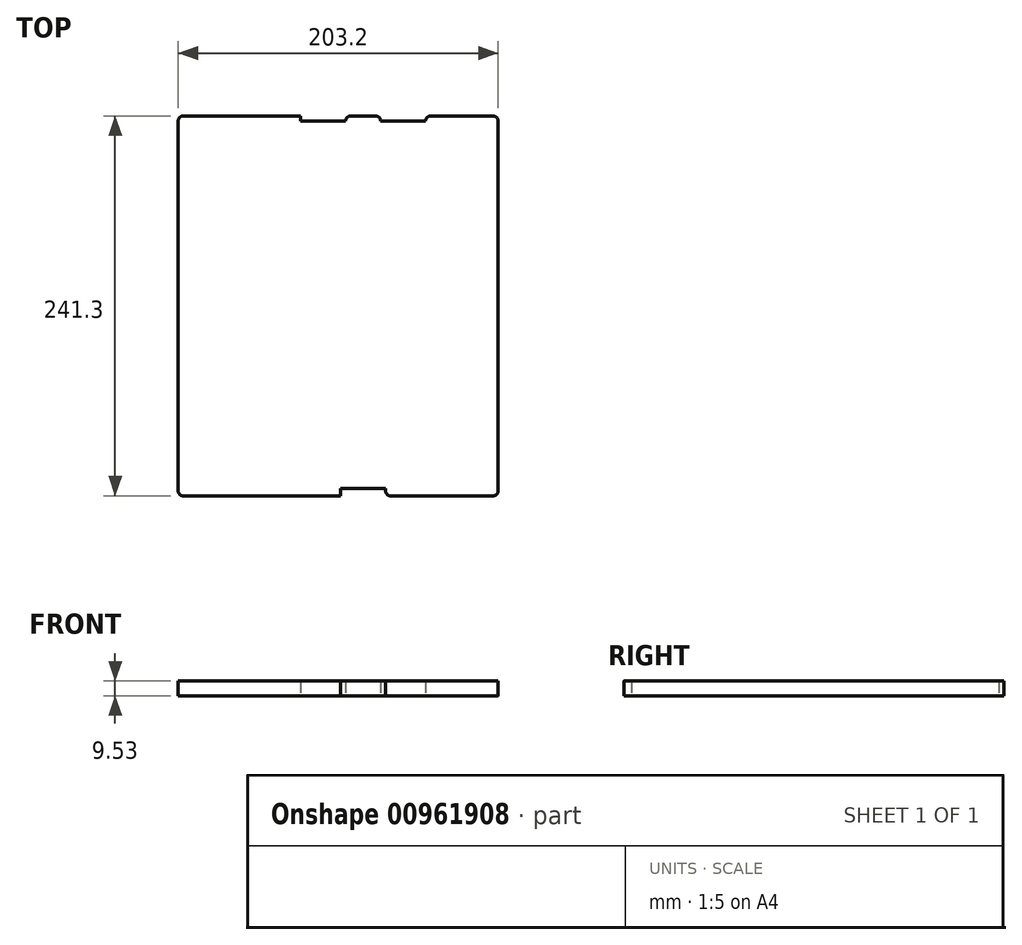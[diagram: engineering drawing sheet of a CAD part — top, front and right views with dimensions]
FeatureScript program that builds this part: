
annotation { "Feature Type Name" : "Feature", "Feature Type Description" : "" }
export const myFeature = defineFeature(function(context is Context, id is Id, definition is map)
    precondition{}
    {
        {
            var Q0;
            Q0=qCreatedBy(makeId("Top.planeOp"),FACE);
            var sketch = newSketch(context, id + "F0", { "sketchPlane" : qUnion([Q0])});
            skLineSegment(sketch, "E0.bottom", {"start": v(101.6, 120.65) * mm, "end": v(-101.6, 120.65) * mm});
            skLineSegment(sketch, "E0.top", {"start": v(101.6, -120.65) * mm, "end": v(-101.6, -120.65) * mm});
            skLineSegment(sketch, "E0.left", {"start": v(101.6, 120.65) * mm, "end": v(101.6, -120.65) * mm});
            skLineSegment(sketch, "E0.right", {"start": v(-101.6, 120.65) * mm, "end": v(-101.6, -120.65) * mm});
            skPoint(sketch, "E0.middle", {"position": v(0, 0) * mm});
            skSolve(sketch);
        }
        {
            var Q0;
            Q0=makeQuery(id+"F0.imprint","IMPRINT",FACE,{"disambiguationData":[TD([[makeQuery(id+"F0.imprint","IMPRINT",EDGE,{"derivedFrom":sQuery(id+"F0.wireOp",EDGE,"E0.bottom")}),1.0]])]});
            extrude(context, id + "F1", {"entities" : qUnion([Q0]), "depth" : 9.52 * mm, "offsetDistance" : 25.4 * mm});
        }
        {
            var Q0;
            Q0=makeQuery(id+"F1.opExtrude","SWEPT_FACE",FACE,{"disambiguationData":[OSD([sQuery(id+"F0.wireOp",EDGE,"E0.top")])]});
            var sketch = newSketch(context, id + "F2", { "sketchPlane" : qUnion([Q0])});
            skLineSegment(sketch, "E1.bottom", {"start": v(1.59, 9.53) * mm, "end": v(30.16, 9.53) * mm});
            skLineSegment(sketch, "E1.top", {"start": v(1.59, 0) * mm, "end": v(30.16, 0) * mm});
            skLineSegment(sketch, "E1.left", {"start": v(1.59, 9.53) * mm, "end": v(1.59, 0) * mm});
            skLineSegment(sketch, "E1.right", {"start": v(30.16, 9.53) * mm, "end": v(30.16, 0) * mm});
            skSolve(sketch);
        }
        {
            var Q0;
            Q0 = qSketchRegion(id + "F2", true);
            extrude(context, id + "F3", {"entities" : qUnion([Q0]), "operationType" : NewBodyOperationType.REMOVE, "oppositeDirection" : true, "depth" : 4.76 * mm, "offsetDistance" : 25.4 * mm});
        }
        {
            var Q0;
            Q0=makeQuery(id+"F1.opExtrude","SWEPT_FACE",FACE,{"disambiguationData":[OSD([sQuery(id+"F0.wireOp",EDGE,"E0.bottom")])]});
            var sketch = newSketch(context, id + "F4", { "sketchPlane" : qUnion([Q0])});
            skLineSegment(sketch, "E2.bottom", {"start": v(-55.56, 9.53) * mm, "end": v(-26.99, 9.53) * mm});
            skLineSegment(sketch, "E2.top", {"start": v(-55.56, 0) * mm, "end": v(-26.99, 0) * mm});
            skLineSegment(sketch, "E2.left", {"start": v(-55.56, 9.53) * mm, "end": v(-55.56, 0) * mm});
            skLineSegment(sketch, "E2.right", {"start": v(-26.99, 9.53) * mm, "end": v(-26.99, 0) * mm});
            skLineSegment(sketch, "E3.bottom", {"start": v(-4.76, 9.53) * mm, "end": v(23.81, 9.53) * mm});
            skLineSegment(sketch, "E3.top", {"start": v(-4.76, 0) * mm, "end": v(23.81, 0) * mm});
            skLineSegment(sketch, "E3.left", {"start": v(-4.76, 9.53) * mm, "end": v(-4.76, 0) * mm});
            skLineSegment(sketch, "E3.right", {"start": v(23.81, 9.53) * mm, "end": v(23.81, 0) * mm});
            skSolve(sketch);
        }
        {
            var Q0;
            Q0=makeQuery(id+"F4.imprint","IMPRINT",FACE,{"disambiguationData":[TD([[makeQuery(id+"F4.imprint","IMPRINT",EDGE,{"derivedFrom":sQuery(id+"F4.wireOp",EDGE,"E2.bottom")}),-1.0]])]});
            var Q1;
            Q1=makeQuery(id+"F4.imprint","IMPRINT",FACE,{"disambiguationData":[TD([[makeQuery(id+"F4.imprint","IMPRINT",EDGE,{"derivedFrom":sQuery(id+"F4.wireOp",EDGE,"E3.bottom")}),-1.0]])]});
            extrude(context, id + "F5", {"entities" : qUnion([Q0, Q1]), "operationType" : NewBodyOperationType.REMOVE, "oppositeDirection" : true, "depth" : 3.17 * mm, "offsetDistance" : 25.4 * mm});
        }
        {
            var Q0;
            Q0=makeQuery(id+"F1.opExtrude","SWEPT_EDGE",EDGE,{"disambiguationData":[OSD([sQuery(id+"F0.wireOp",EDGE,"E0.bottom"),sQuery(id+"F0.wireOp",EDGE,"E0.right")])]});
            var Q1;
            Q1=makeQuery(id+"F5.boolean.opBoolean","COPY",EDGE,{"derivedFrom":makeQuery(id+"F5.opExtrude","CAP_EDGE",EDGE,{"disambiguationData":[OSD([sQuery(id+"F4.wireOp",EDGE,"E3.right")])],"isStart":true})});
            var Q2;
            Q2=makeQuery(id+"F5.boolean.opBoolean","COPY",EDGE,{"derivedFrom":makeQuery(id+"F5.opExtrude","CAP_EDGE",EDGE,{"disambiguationData":[OSD([sQuery(id+"F4.wireOp",EDGE,"E3.left")])],"isStart":true})});
            var Q3;
            Q3=makeQuery(id+"F5.boolean.opBoolean","COPY",EDGE,{"derivedFrom":makeQuery(id+"F5.opExtrude","CAP_EDGE",EDGE,{"disambiguationData":[OSD([sQuery(id+"F4.wireOp",EDGE,"E2.right")])],"isStart":true})});
            var Q4;
            Q4=makeQuery(id+"F5.boolean.opBoolean","COPY",EDGE,{"derivedFrom":makeQuery(id+"F5.opExtrude","CAP_EDGE",EDGE,{"disambiguationData":[OSD([sQuery(id+"F4.wireOp",EDGE,"E2.left")])],"isStart":true})});
            var Q5;
            Q5=makeQuery(id+"F1.opExtrude","SWEPT_EDGE",EDGE,{"disambiguationData":[OSD([sQuery(id+"F0.wireOp",EDGE,"E0.bottom"),sQuery(id+"F0.wireOp",EDGE,"E0.left")])]});
            var Q6;
            Q6=makeQuery(id+"F1.opExtrude","SWEPT_EDGE",EDGE,{"disambiguationData":[OSD([sQuery(id+"F0.wireOp",EDGE,"E0.top"),sQuery(id+"F0.wireOp",EDGE,"E0.right")])]});
            var Q7;
            Q7=makeQuery(id+"F3.boolean.opBoolean","COPY",EDGE,{"derivedFrom":makeQuery(id+"F3.opExtrude","CAP_EDGE",EDGE,{"disambiguationData":[OSD([sQuery(id+"F2.wireOp",EDGE,"E1.left")])],"isStart":true})});
            var Q8;
            Q8=makeQuery(id+"F3.boolean.opBoolean","COPY",EDGE,{"derivedFrom":makeQuery(id+"F3.opExtrude","CAP_EDGE",EDGE,{"disambiguationData":[OSD([sQuery(id+"F2.wireOp",EDGE,"E1.right")])],"isStart":true})});
            var Q9;
            Q9=makeQuery(id+"F1.opExtrude","SWEPT_EDGE",EDGE,{"disambiguationData":[OSD([sQuery(id+"F0.wireOp",EDGE,"E0.top"),sQuery(id+"F0.wireOp",EDGE,"E0.left")])]});
            fillet(context, id + "F6", {"entities" : qUnion([Q0, Q1, Q2, Q3, Q4, Q5, Q6, Q7, Q8, Q9]), "radius" : 3.17 * mm, "tangentPropagation" : true, "allowEdgeOverflow" : false});
        }
    });
